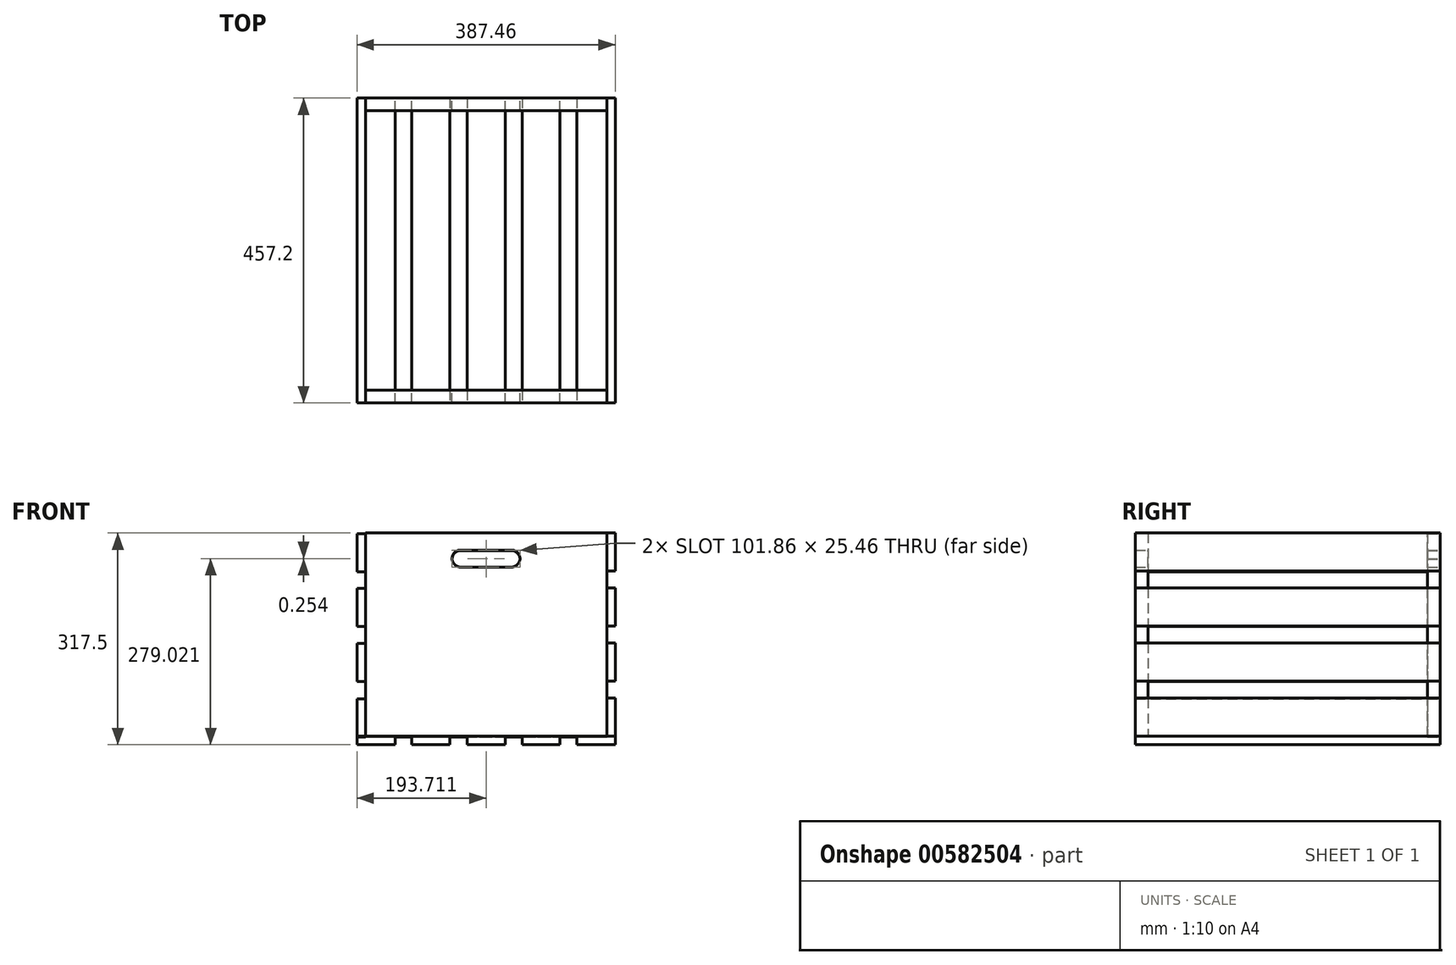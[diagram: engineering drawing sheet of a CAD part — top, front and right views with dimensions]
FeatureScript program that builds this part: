
annotation { "Feature Type Name" : "Feature", "Feature Type Description" : "" }
export const myFeature = defineFeature(function(context is Context, id is Id, definition is map)
    precondition{}
    {
        {
            var Q0;
            Q0=qCreatedBy(makeId("Front.planeOp"),FACE);
            var sketch = newSketch(context, id + "F0", { "sketchPlane" : qUnion([Q0])});
            skLineSegment(sketch, "E0", {"start": v(-180.98, 152.4) * mm, "end": v(180.98, 152.4) * mm});
            skLineSegment(sketch, "E1", {"start": v(-180.98, 152.4) * mm, "end": v(-180.98, -152.4) * mm});
            skLineSegment(sketch, "E2", {"start": v(180.98, 152.4) * mm, "end": v(180.98, -152.4) * mm});
            skLineSegment(sketch, "E3", {"start": v(-180.98, -152.4) * mm, "end": v(180.98, -152.4) * mm});
            skPoint(sketch, "E4.endSnap0", {"position": v(0, 152.4) * mm});
            skArc(sketch, "E5", {"start": v(-38.27, 126.9) * mm, "mid": v(-51, 114.17) * mm, "end": v(-38.27, 101.44) * mm});
            skArc(sketch, "E6", {"start": v(38.13, 126.9) * mm, "mid": v(50.86, 114.17) * mm, "end": v(38.13, 101.44) * mm});
            skLineSegment(sketch, "E7", {"start": v(-38.27, 126.9) * mm, "end": v(38.13, 126.9) * mm});
            skLineSegment(sketch, "E8", {"start": v(-38.27, 101.44) * mm, "end": v(38.13, 101.44) * mm});
            skSolve(sketch);
        }
        {
            var Q0;
            Q0 = qSketchRegion(id + "F0", true);
            extrude(context, id + "F1", {"entities" : qUnion([Q0]), "depth" : 19.05 * mm, "offsetDistance" : 25.4 * mm});
        }
        {
            var Q0;
            Q0=qCreatedBy(makeId("Front.planeOp"),FACE);
            var sketch = newSketch(context, id + "F2", { "sketchPlane" : qUnion([Q0])});
            skLineSegment(sketch, "E9", {"start": v(-180.94, 153.3) * mm, "end": v(181, 153.3) * mm});
            skLineSegment(sketch, "E10", {"start": v(-180.94, 153.3) * mm, "end": v(-180.94, -151.5) * mm});
            skLineSegment(sketch, "E11", {"start": v(181, 153.3) * mm, "end": v(181, -151.5) * mm});
            skLineSegment(sketch, "E12", {"start": v(-180.94, -151.5) * mm, "end": v(181, -151.5) * mm});
            skPoint(sketch, "E13.endSnap0", {"position": v(0.03, 153.3) * mm});
            skArc(sketch, "E14", {"start": v(-38.23, 127.8) * mm, "mid": v(-50.97, 115.08) * mm, "end": v(-38.23, 102.34) * mm});
            skArc(sketch, "E15", {"start": v(38.16, 127.8) * mm, "mid": v(50.89, 115.08) * mm, "end": v(38.16, 102.34) * mm});
            skLineSegment(sketch, "E16", {"start": v(-38.23, 127.8) * mm, "end": v(38.16, 127.8) * mm});
            skLineSegment(sketch, "E17", {"start": v(-38.23, 102.34) * mm, "end": v(38.16, 102.34) * mm});
            skSolve(sketch);
        }
        {
            var Q0;
            Q0 = qSketchRegion(id + "F2", true);
            extrude(context, id + "F3", {"entities" : qUnion([Q0]), "operationType" : NewBodyOperationType.ADD, "depth" : 457.2 * mm, "offsetDistance" : 25.4 * mm});
        }
        {
            var Q0;
            Q0=qCreatedBy(makeId("Front.planeOp"),FACE);
            var sketch = newSketch(context, id + "F4", { "sketchPlane" : qUnion([Q0])});
            skLineSegment(sketch, "E18", {"start": v(-180.94, 153.3) * mm, "end": v(181, 153.3) * mm});
            skLineSegment(sketch, "E19", {"start": v(-180.94, 153.3) * mm, "end": v(-180.94, -151.5) * mm});
            skLineSegment(sketch, "E20", {"start": v(181, 153.3) * mm, "end": v(181, -151.5) * mm});
            skLineSegment(sketch, "E21", {"start": v(-180.94, -151.5) * mm, "end": v(181, -151.5) * mm});
            skPoint(sketch, "E22.endSnap0", {"position": v(0.03, 153.3) * mm});
            skArc(sketch, "E23", {"start": v(-38.23, 127.8) * mm, "mid": v(-50.97, 115.08) * mm, "end": v(-38.23, 102.34) * mm});
            skArc(sketch, "E24", {"start": v(38.16, 127.8) * mm, "mid": v(50.89, 115.08) * mm, "end": v(38.16, 102.34) * mm});
            skLineSegment(sketch, "E25", {"start": v(-38.23, 127.8) * mm, "end": v(38.16, 127.8) * mm});
            skLineSegment(sketch, "E26", {"start": v(-38.23, 102.34) * mm, "end": v(38.16, 102.34) * mm});
            skSolve(sketch);
        }
        {
            var Q0;
            Q0 = qSketchRegion(id + "F4", true);
            extrude(context, id + "F5", {"entities" : qUnion([Q0]), "operationType" : NewBodyOperationType.REMOVE, "depth" : 438.15 * mm, "offsetDistance" : 25.4 * mm});
        }
        {
            var Q0;
            Q0=qCreatedBy(makeId("Front.planeOp"),FACE);
            var sketch = newSketch(context, id + "F6", { "sketchPlane" : qUnion([Q0])});
            skLineSegment(sketch, "E27", {"start": v(-180.94, 153.05) * mm, "end": v(181, 153.05) * mm});
            skLineSegment(sketch, "E28", {"start": v(-180.94, 153.05) * mm, "end": v(-180.94, -151.75) * mm});
            skLineSegment(sketch, "E29", {"start": v(181, 153.05) * mm, "end": v(181, -151.75) * mm});
            skLineSegment(sketch, "E30", {"start": v(-180.94, -151.75) * mm, "end": v(181, -151.75) * mm});
            skPoint(sketch, "E31.endSnap0", {"position": v(0.03, 153.05) * mm});
            skArc(sketch, "E32", {"start": v(-38.23, 127.55) * mm, "mid": v(-50.97, 114.82) * mm, "end": v(-38.23, 102.09) * mm});
            skArc(sketch, "E33", {"start": v(38.16, 127.55) * mm, "mid": v(50.89, 114.82) * mm, "end": v(38.16, 102.09) * mm});
            skLineSegment(sketch, "E34", {"start": v(-38.23, 127.55) * mm, "end": v(38.16, 127.55) * mm});
            skLineSegment(sketch, "E35", {"start": v(-38.23, 102.09) * mm, "end": v(38.16, 102.09) * mm});
            skSolve(sketch);
        }
        {
            var Q0;
            Q0 = qSketchRegion(id + "F6", true);
            extrude(context, id + "F7", {"entities" : qUnion([Q0]), "depth" : 19.05 * mm, "offsetDistance" : 25.4 * mm});
        }
        {
            var Q0;
            Q0=makeQuery(id+"F3.opExtrude","SWEPT_FACE",FACE,{"disambiguationData":[OSD([sQuery(id+"F2.wireOp",EDGE,"E11")])]});
            var sketch = newSketch(context, id + "F8", { "sketchPlane" : qUnion([Q0])});
            skLineSegment(sketch, "E36", {"start": v(-457.2, 153.3) * mm, "end": v(0, 153.3) * mm});
            skLineSegment(sketch, "E37", {"start": v(-457.2, 153.3) * mm, "end": v(-457.2, 96.15) * mm});
            skLineSegment(sketch, "E38", {"start": v(-457.2, 96.15) * mm, "end": v(0, 96.15) * mm});
            skLineSegment(sketch, "E39", {"start": v(0, 96.15) * mm, "end": v(0, 153.3) * mm});
            skLineSegment(sketch, "E40", {"start": v(-457.2, -151.5) * mm, "end": v(0, -151.5) * mm});
            skLineSegment(sketch, "E41", {"start": v(0, -151.5) * mm, "end": v(0, -94.35) * mm});
            skLineSegment(sketch, "E42", {"start": v(0, -94.35) * mm, "end": v(-457.2, -94.35) * mm});
            skLineSegment(sketch, "E43", {"start": v(-457.2, -94.35) * mm, "end": v(-457.2, -151.5) * mm});
            skLineSegment(sketch, "E44", {"start": v(-457.2, 71.01) * mm, "end": v(0, 71.01) * mm});
            skLineSegment(sketch, "E45", {"start": v(0, 71.01) * mm, "end": v(0, 13.86) * mm});
            skLineSegment(sketch, "E46", {"start": v(0, 13.86) * mm, "end": v(-457.2, 13.86) * mm});
            skLineSegment(sketch, "E47", {"start": v(-457.2, 13.86) * mm, "end": v(-457.2, 71.01) * mm});
            skLineSegment(sketch, "E48", {"start": v(-457.2, 71.01) * mm, "end": v(-457.2, -11.54) * mm});
            skLineSegment(sketch, "E49", {"start": v(-457.2, -11.54) * mm, "end": v(0, -11.54) * mm});
            skLineSegment(sketch, "E50", {"start": v(0, -11.54) * mm, "end": v(0, -68.69) * mm});
            skLineSegment(sketch, "E51", {"start": v(0, -68.69) * mm, "end": v(-457.2, -68.69) * mm});
            skLineSegment(sketch, "E52", {"start": v(-457.2, -68.69) * mm, "end": v(-457.2, -11.54) * mm});
            skSolve(sketch);
        }
        {
            var Q0;
            Q0 = qSketchRegion(id + "F8", true);
            extrude(context, id + "F9", {"entities" : qUnion([Q0]), "depth" : 12.7 * mm, "offsetDistance" : 25.4 * mm});
        }
        {
            var Q0;
            Q0 = qSketchRegion(id + "F8", true);
            extrude(context, id + "F10", {"entities" : qUnion([Q0]), "depth" : 12.7 * mm, "offsetDistance" : 25.4 * mm});
        }
        {
            var Q0;
            Q0=makeQuery(id+"F1.opExtrude","SWEPT_FACE",FACE,{"disambiguationData":[OSD([sQuery(id+"F0.wireOp",EDGE,"E1")])]});
            var sketch = newSketch(context, id + "F11", { "sketchPlane" : qUnion([Q0])});
            skLineSegment(sketch, "E53", {"start": v(0, 152.4) * mm, "end": v(457.2, 152.4) * mm});
            skLineSegment(sketch, "E54", {"start": v(0, 152.4) * mm, "end": v(0, 95.25) * mm});
            skLineSegment(sketch, "E55", {"start": v(0, 95.25) * mm, "end": v(457.2, 95.25) * mm});
            skLineSegment(sketch, "E56", {"start": v(457.2, 95.25) * mm, "end": v(457.2, 152.4) * mm});
            skLineSegment(sketch, "E57", {"start": v(0, -152.4) * mm, "end": v(457.2, -152.4) * mm});
            skLineSegment(sketch, "E58", {"start": v(457.2, -152.4) * mm, "end": v(457.2, -95.25) * mm});
            skLineSegment(sketch, "E59", {"start": v(457.2, -95.25) * mm, "end": v(0, -95.25) * mm});
            skLineSegment(sketch, "E60", {"start": v(0, -95.25) * mm, "end": v(0, -152.4) * mm});
            skLineSegment(sketch, "E61", {"start": v(0, 70.1) * mm, "end": v(457.2, 70.1) * mm});
            skLineSegment(sketch, "E62", {"start": v(457.2, 70.1) * mm, "end": v(457.2, 12.96) * mm});
            skLineSegment(sketch, "E63", {"start": v(457.2, 12.96) * mm, "end": v(0, 12.96) * mm});
            skLineSegment(sketch, "E64", {"start": v(0, 12.96) * mm, "end": v(0, 70.1) * mm});
            skLineSegment(sketch, "E65", {"start": v(0, 70.1) * mm, "end": v(0, -12.44) * mm});
            skLineSegment(sketch, "E66", {"start": v(0, -12.44) * mm, "end": v(457.2, -12.44) * mm});
            skLineSegment(sketch, "E67", {"start": v(457.2, -12.44) * mm, "end": v(457.2, -69.6) * mm});
            skLineSegment(sketch, "E68", {"start": v(457.2, -69.6) * mm, "end": v(0, -69.6) * mm});
            skLineSegment(sketch, "E69", {"start": v(0, -69.6) * mm, "end": v(0, -12.44) * mm});
            skSolve(sketch);
        }
        {
            var Q0;
            Q0 = qSketchRegion(id + "F11", true);
            extrude(context, id + "F12", {"entities" : qUnion([Q0]), "operationType" : NewBodyOperationType.ADD, "depth" : 12.7 * mm, "offsetDistance" : 25.4 * mm});
        }
        {
            var Q0;
            Q0=makeQuery(id+"F3.opExtrude","SWEPT_FACE",FACE,{"disambiguationData":[OSD([sQuery(id+"F2.wireOp",EDGE,"E12")])]});
            var sketch = newSketch(context, id + "F13", { "sketchPlane" : qUnion([Q0])});
            skLineSegment(sketch, "E70", {"start": v(-193.75, 457.2) * mm, "end": v(-136.6, 457.2) * mm});
            skLineSegment(sketch, "E71", {"start": v(-136.6, 457.2) * mm, "end": v(-136.6, 0) * mm});
            skPoint(sketch, "E72.endSnap0", {"position": v(-165.17, 457.2) * mm});
            skLineSegment(sketch, "E73", {"start": v(-193.75, 0) * mm, "end": v(-193.75, 457.2) * mm});
            skLineSegment(sketch, "E74", {"start": v(-136.6, 0) * mm, "end": v(-193.75, 0) * mm});
            skLineSegment(sketch, "E75", {"start": v(-111.2, 457.2) * mm, "end": v(-111.2, 0) * mm});
            skLineSegment(sketch, "E76", {"start": v(-111.2, 0) * mm, "end": v(-54.05, 0) * mm});
            skLineSegment(sketch, "E77", {"start": v(-54.05, 0) * mm, "end": v(-54.05, 457.2) * mm});
            skLineSegment(sketch, "E78", {"start": v(-54.05, 457.2) * mm, "end": v(-111.2, 457.2) * mm});
            skLineSegment(sketch, "E79", {"start": v(-28.65, 0) * mm, "end": v(-28.65, 457.2) * mm});
            skPoint(sketch, "E79.endSnap0", {"position": v(0.03, 457.2) * mm});
            skLineSegment(sketch, "E80", {"start": v(-28.65, 457.2) * mm, "end": v(28.5, 457.2) * mm});
            skLineSegment(sketch, "E81", {"start": v(28.5, 457.2) * mm, "end": v(28.5, 0) * mm});
            skLineSegment(sketch, "E82", {"start": v(28.5, 0) * mm, "end": v(-28.65, 0) * mm});
            skLineSegment(sketch, "E83", {"start": v(53.9, 0) * mm, "end": v(53.9, 457.2) * mm});
            skLineSegment(sketch, "E84", {"start": v(53.9, 457.2) * mm, "end": v(111.05, 457.2) * mm});
            skLineSegment(sketch, "E85", {"start": v(111.05, 457.2) * mm, "end": v(111.05, 0) * mm});
            skLineSegment(sketch, "E86", {"start": v(111.05, 0) * mm, "end": v(53.9, 0) * mm});
            skPoint(sketch, "E87.endSnap0", {"position": v(82.48, 0) * mm});
            skLineSegment(sketch, "E88", {"start": v(136.45, 0) * mm, "end": v(136.45, 457.2) * mm});
            skLineSegment(sketch, "E89", {"start": v(136.45, 457.2) * mm, "end": v(193.6, 457.2) * mm});
            skLineSegment(sketch, "E90", {"start": v(193.6, 457.2) * mm, "end": v(193.6, 0) * mm});
            skLineSegment(sketch, "E91", {"start": v(193.6, 0) * mm, "end": v(136.45, 0) * mm});
            skSolve(sketch);
        }
        {
            var Q0;
            Q0 = qSketchRegion(id + "F13", true);
            extrude(context, id + "F14", {"entities" : qUnion([Q0]), "depth" : 12.7 * mm, "offsetDistance" : 25.4 * mm});
        }
    });
